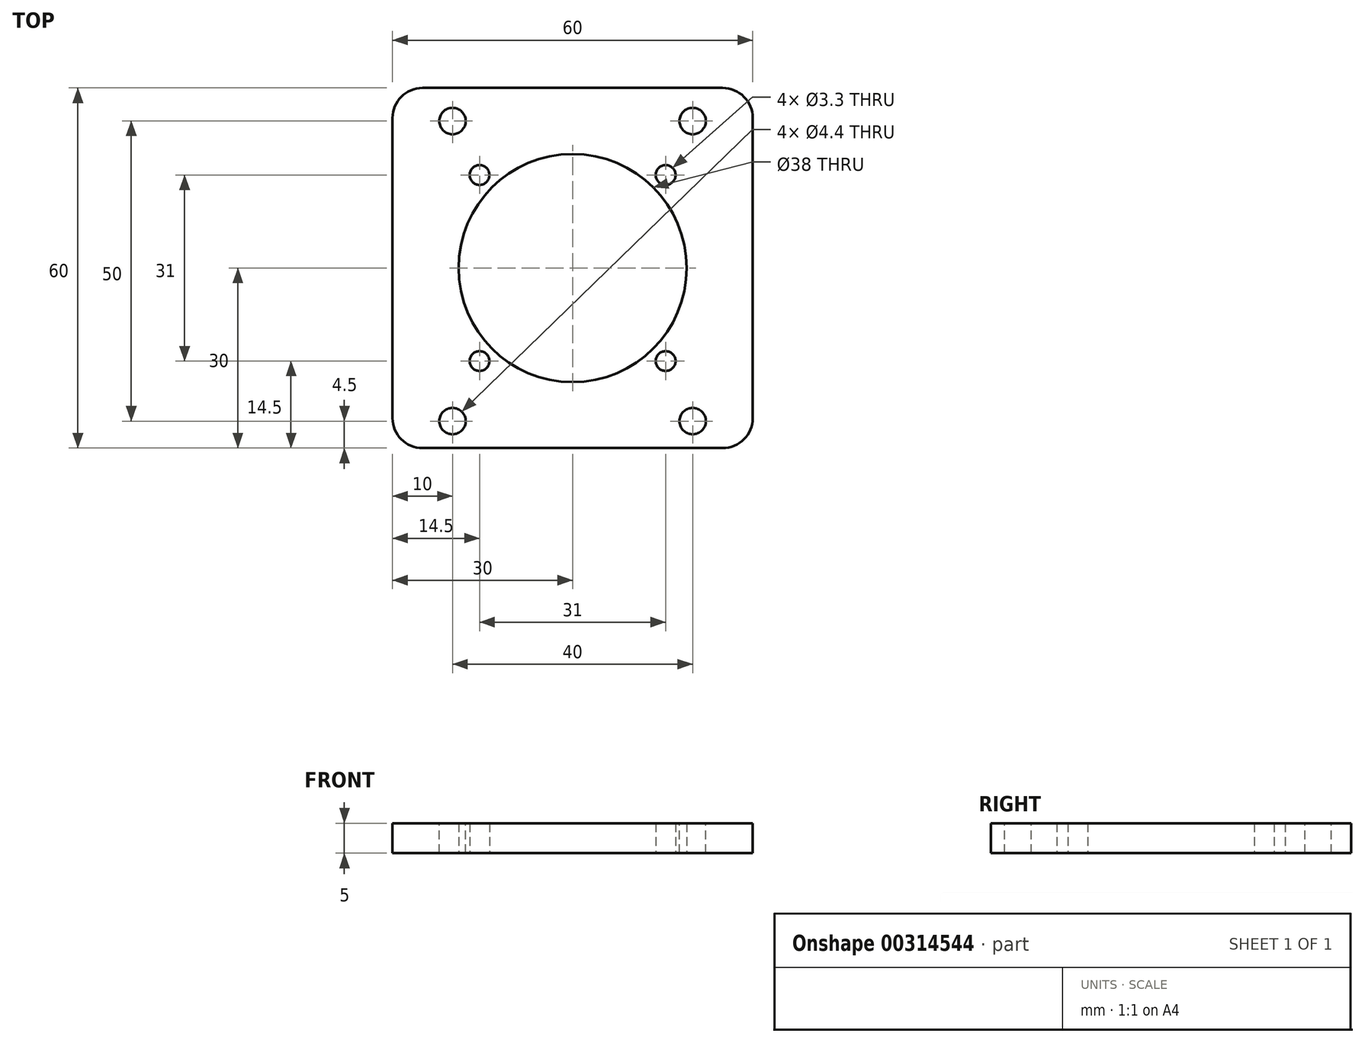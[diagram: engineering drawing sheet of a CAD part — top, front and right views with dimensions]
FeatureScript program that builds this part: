
annotation { "Feature Type Name" : "Feature", "Feature Type Description" : "" }
export const myFeature = defineFeature(function(context is Context, id is Id, definition is map)
    precondition{}
    {
        {
            var Q0;
            Q0=qCreatedBy(makeId("Top.planeOp"),FACE);
            var sketch = newSketch(context, id + "F0", { "sketchPlane" : qUnion([Q0])});
            skLineSegment(sketch, "E0.bottom", {"start": v(30, 30) * mm, "end": v(-30, 30) * mm});
            skLineSegment(sketch, "E0.top", {"start": v(30, -30) * mm, "end": v(-30, -30) * mm});
            skLineSegment(sketch, "E0.left", {"start": v(30, 30) * mm, "end": v(30, -30) * mm});
            skLineSegment(sketch, "E0.right", {"start": v(-30, 30) * mm, "end": v(-30, -30) * mm});
            skPoint(sketch, "E0.middle", {"position": v(0, 0) * mm});
            skCircle(sketch, "E1", {"center": v(0, 0) * mm, "radius": 19 * mm});
            skLineSegment(sketch, "E2.bottom", {"start": v(-15.5, 15.5) * mm, "end": v(15.5, 15.5) * mm, "construction": true});
            skLineSegment(sketch, "E2.top", {"start": v(-15.5, -15.5) * mm, "end": v(15.5, -15.5) * mm, "construction": true});
            skLineSegment(sketch, "E2.left", {"start": v(-15.5, 15.5) * mm, "end": v(-15.5, -15.5) * mm, "construction": true});
            skLineSegment(sketch, "E2.right", {"start": v(15.5, 15.5) * mm, "end": v(15.5, -15.5) * mm, "construction": true});
            skSolve(sketch);
        }
        {
            var Q0;
            Q0 = qSketchRegion(id + "F0", true);
            extrude(context, id + "F1", {"entities" : qUnion([Q0]), "depth" : 5 * mm});
        }
        {
            var Q0;
            Q0=sQuery(id+"F0.wireOp",VERTEX,"E2.left.start");
            var Q1;
            Q1=sQuery(id+"F0.wireOp",VERTEX,"E2.right.start");
            var Q2;
            Q2=sQuery(id+"F0.wireOp",VERTEX,"E2.right.end");
            var Q3;
            Q3=sQuery(id+"F0.wireOp",VERTEX,"E2.left.end");
            var Q4;
            Q4=makeQuery(id+"F1.opExtrude","SWEPT_BODY",BODY,{"disambiguationData":[OSD([sQuery(id+"F0.wireOp",EDGE,"E0.bottom"),sQuery(id+"F0.wireOp",EDGE,"E0.top"),sQuery(id+"F0.wireOp",EDGE,"E0.left"),sQuery(id+"F0.wireOp",EDGE,"E0.right"),sQuery(id+"F0.wireOp",EDGE,"E1")])]});
            hole(context, id + "F2", {"style" : HoleStyle.SIMPLE, "endStyle" : HoleEndStyle.BLIND, "oppositeDirection" : true, "standardTappedOrClearance" : lookupTablePath({ "standard" : "ISO", "fit" : "Normal", "size" : "M3", "type" : "Clearance" }), "standardBlindInLast" : lookupTablePath({ "fit" : "Standard", "standard" : "ISO", "size" : "M3", "type" : "Clearance" }), "holeDiameter" : 3.3 * mm, "holeDepth" : 13.8 * mm, "tappedDepth" : 12 * mm, "tapClearance" : 3, "locations" : qUnion([Q0, Q1, Q2, Q3]), "scope" : qUnion([Q4])});
        }
        {
            var Q0;
            Q0=makeQuery(id+"F1.opExtrude","CAP_FACE",FACE,{"disambiguationData":[OSD([sQuery(id+"F0.wireOp",EDGE,"E0.bottom"),sQuery(id+"F0.wireOp",EDGE,"E0.top"),sQuery(id+"F0.wireOp",EDGE,"E0.left"),sQuery(id+"F0.wireOp",EDGE,"E0.right"),sQuery(id+"F0.wireOp",EDGE,"E1")])],"isStart":false});
            var sketch = newSketch(context, id + "F3", { "sketchPlane" : qUnion([Q0])});
            skPoint(sketch, "E3", {"position": v(-20, 24.5) * mm});
            skPoint(sketch, "E4.0.1.0", {"position": v(-20, -25.5) * mm});
            skPoint(sketch, "E4.1.0.0", {"position": v(20, 24.5) * mm});
            skPoint(sketch, "E4.1.1.0", {"position": v(20, -25.5) * mm});
            skLineSegment(sketch, "E4.direction1", {"start": v(-24, 20) * mm, "end": v(16, 20) * mm, "construction": true});
            skLineSegment(sketch, "E4.direction2", {"start": v(-24, 20) * mm, "end": v(-24, -30) * mm, "construction": true});
            skSolve(sketch);
        }
        {
            var Q0;
            Q0=sQuery(id+"F3.wireOp",VERTEX,"E3");
            var Q1;
            Q1=sQuery(id+"F3.wireOp",VERTEX,"E4.1.0.0");
            var Q2;
            Q2=sQuery(id+"F3.wireOp",VERTEX,"E4.1.1.0");
            var Q3;
            Q3=sQuery(id+"F3.wireOp",VERTEX,"E4.0.1.0");
            var Q4;
            Q4=makeQuery(id+"F1.opExtrude","SWEPT_BODY",BODY,{"disambiguationData":[OSD([sQuery(id+"F0.wireOp",EDGE,"E0.bottom"),sQuery(id+"F0.wireOp",EDGE,"E0.top"),sQuery(id+"F0.wireOp",EDGE,"E0.left"),sQuery(id+"F0.wireOp",EDGE,"E0.right"),sQuery(id+"F0.wireOp",EDGE,"E1")])]});
            hole(context, id + "F4", {"style" : HoleStyle.SIMPLE, "endStyle" : HoleEndStyle.BLIND, "standardTappedOrClearance" : lookupTablePath({ "standard" : "ISO", "fit" : "Normal", "size" : "M4", "type" : "Clearance" }), "standardBlindInLast" : lookupTablePath({ "fit" : "Standard", "standard" : "ISO", "size" : "M4", "type" : "Clearance" }), "holeDiameter" : 4.4 * mm, "holeDepth" : 13.8 * mm, "tappedDepth" : 12 * mm, "tapClearance" : 3, "locations" : qUnion([Q0, Q1, Q2, Q3]), "scope" : qUnion([Q4])});
        }
        {
            var Q0;
            Q0=makeQuery(id+"F1.opExtrude","SWEPT_EDGE",EDGE,{"disambiguationData":[OSD([sQuery(id+"F0.wireOp",EDGE,"E0.bottom"),sQuery(id+"F0.wireOp",EDGE,"E0.right")])]});
            var Q1;
            Q1=makeQuery(id+"F1.opExtrude","SWEPT_EDGE",EDGE,{"disambiguationData":[OSD([sQuery(id+"F0.wireOp",EDGE,"E0.bottom"),sQuery(id+"F0.wireOp",EDGE,"E0.left")])]});
            var Q2;
            Q2=makeQuery(id+"F1.opExtrude","SWEPT_EDGE",EDGE,{"disambiguationData":[OSD([sQuery(id+"F0.wireOp",EDGE,"E0.top"),sQuery(id+"F0.wireOp",EDGE,"E0.left")])]});
            var Q3;
            Q3=makeQuery(id+"F1.opExtrude","SWEPT_EDGE",EDGE,{"disambiguationData":[OSD([sQuery(id+"F0.wireOp",EDGE,"E0.top"),sQuery(id+"F0.wireOp",EDGE,"E0.right")])]});
            fillet(context, id + "F5", {"entities" : qUnion([Q0, Q1, Q2, Q3]), "radius" : 5 * mm, "tangentPropagation" : true, "allowEdgeOverflow" : false});
        }
    });
